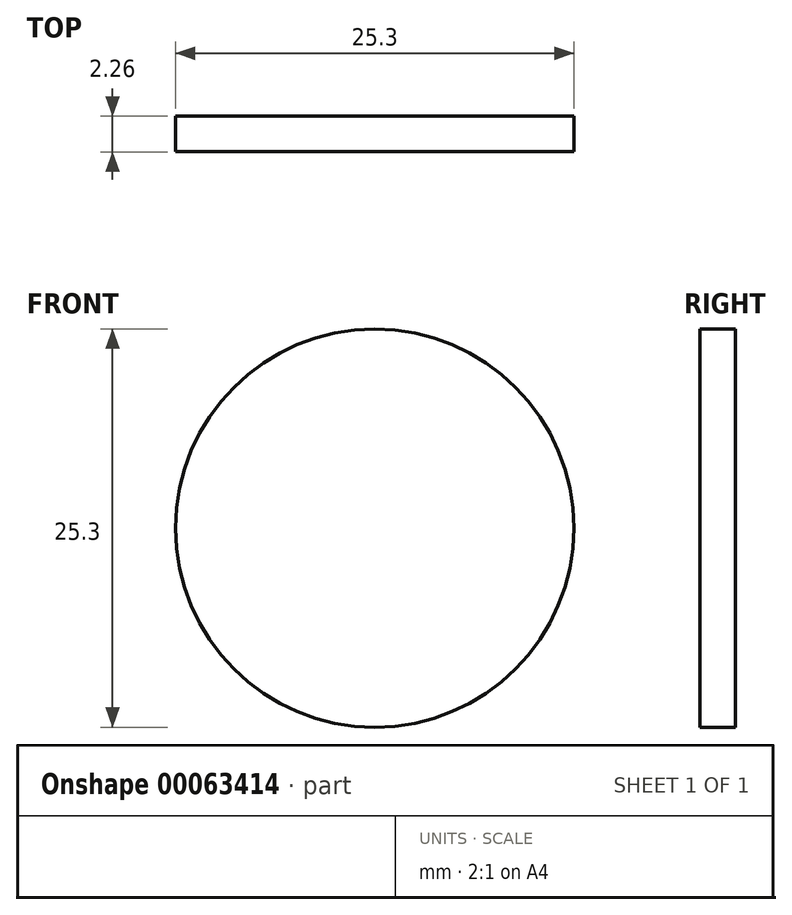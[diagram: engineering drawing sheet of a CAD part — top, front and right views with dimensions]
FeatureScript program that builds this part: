
annotation { "Feature Type Name" : "Feature", "Feature Type Description" : "" }
export const myFeature = defineFeature(function(context is Context, id is Id, definition is map)
    precondition{}
    {
        {
            var Q0;
            Q0=qCreatedBy(makeId("Front.planeOp"),FACE);
            var sketch = newSketch(context, id + "F0", { "sketchPlane" : qUnion([Q0])});
            skCircle(sketch, "E0", {"center": v(0, 0) * mm, "radius": 12.65 * mm});
            skSolve(sketch);
        }
        {
            var Q0;
            Q0 = qSketchRegion(id + "F0", true);
            extrude(context, id + "F1", {"entities" : qUnion([Q0]), "depth" : 2.26 * mm});
        }
    });
